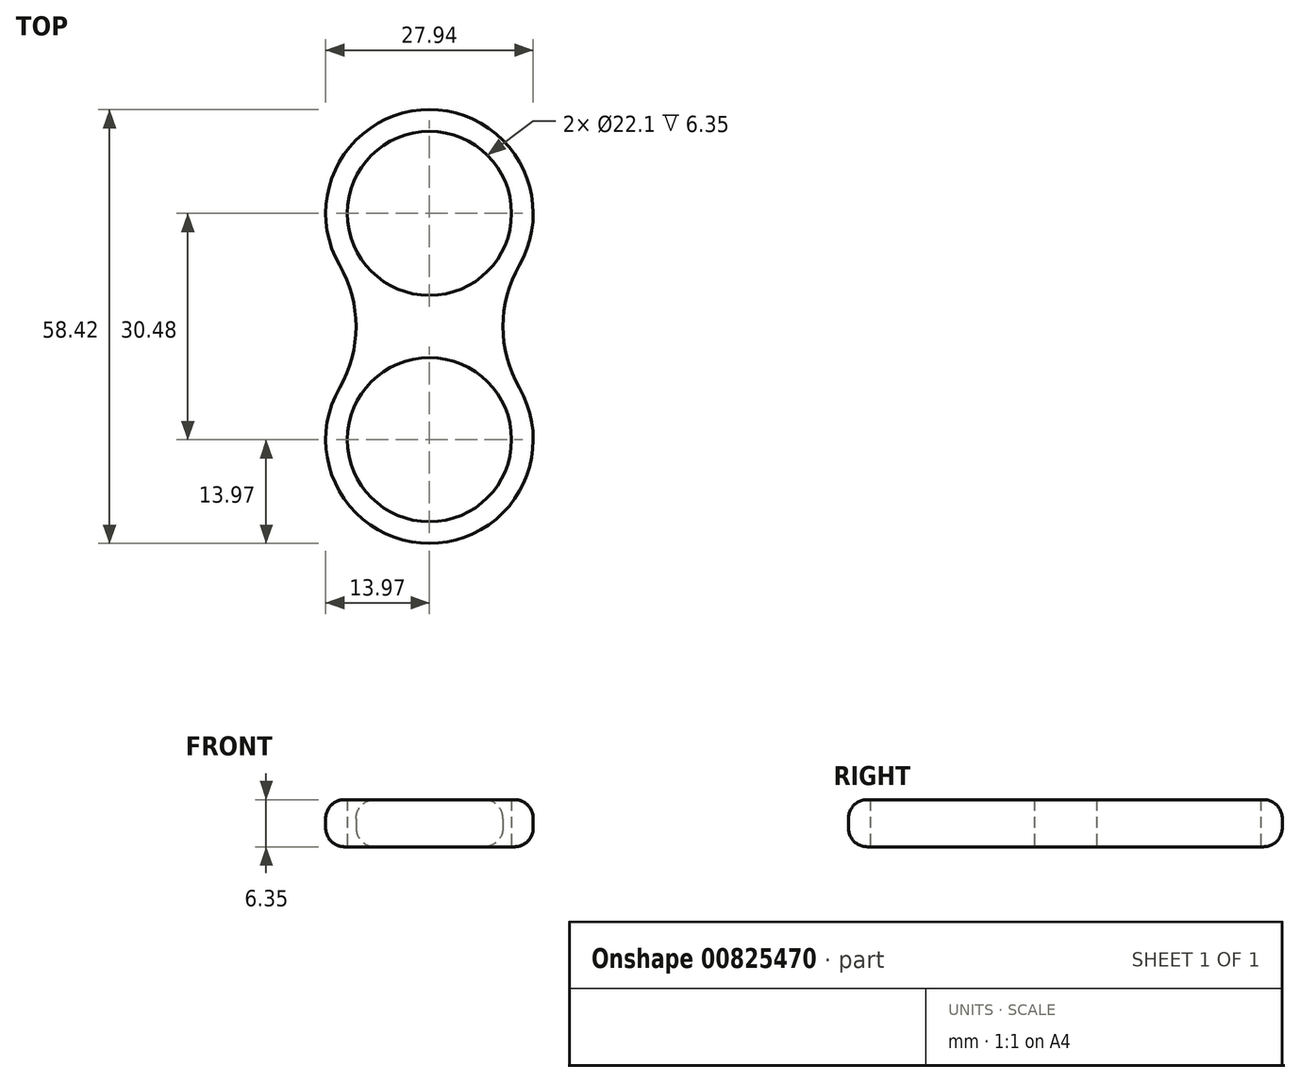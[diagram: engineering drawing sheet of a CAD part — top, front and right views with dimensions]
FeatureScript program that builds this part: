
annotation { "Feature Type Name" : "Feature", "Feature Type Description" : "" }
export const myFeature = defineFeature(function(context is Context, id is Id, definition is map)
    precondition{}
    {
        {
            var Q0;
            Q0=qCreatedBy(makeId("Top.planeOp"),FACE);
            var sketch = newSketch(context, id + "F0", { "sketchPlane" : qUnion([Q0])});
            skCircle(sketch, "E0", {"center": v(0, 0) * mm, "radius": 11.05 * mm});
            skArc(sketch, "E1", {"start": v(-12.1, 6.99) * mm, "mid": v(0, -13.97) * mm, "end": v(12.1, 6.99) * mm});
            skCircle(sketch, "E2", {"center": v(0, 30.48) * mm, "radius": 11.05 * mm});
            skArc(sketch, "E3", {"start": v(12.1, 23.5) * mm, "mid": v(0, 44.45) * mm, "end": v(-12.1, 23.5) * mm});
            skArc(sketch, "E4.trimOffspring", {"start": v(-12.1, 6.98) * mm, "mid": v(-9.89, 15.24) * mm, "end": v(-12.1, 23.5) * mm});
            skArc(sketch, "E5", {"start": v(12.1, 23.5) * mm, "mid": v(9.89, 15.24) * mm, "end": v(12.1, 6.99) * mm});
            skSolve(sketch);
        }
        {
            var Q0;
            Q0=makeQuery(id+"F0.imprint","IMPRINT",FACE,{"disambiguationData":[TD([[makeQuery(id+"F0.imprint","IMPRINT",EDGE,{"derivedFrom":sQuery(id+"F0.wireOp",EDGE,"E0")}),-1.0]])]});
            extrude(context, id + "F1", {"entities" : qUnion([Q0]), "depth" : 6.35 * mm, "offsetDistance" : 25.4 * mm});
        }
        {
            var Q0;
            Q0=makeQuery(id+"F1.opExtrude","CAP_EDGE",EDGE,{"disambiguationData":[OSD([sQuery(id+"F0.wireOp",EDGE,"E1")])],"isStart":false});
            fillet(context, id + "F2", {"entities" : qUnion([Q0]), "radius" : 2.54 * mm, "tangentPropagation" : true, "allowEdgeOverflow" : false});
        }
        {
            var Q0;
            Q0=makeQuery(id+"F1.opExtrude","CAP_EDGE",EDGE,{"disambiguationData":[OSD([sQuery(id+"F0.wireOp",EDGE,"E1")])],"isStart":true});
            fillet(context, id + "F3", {"entities" : qUnion([Q0]), "radius" : 2.54 * mm, "tangentPropagation" : true, "allowEdgeOverflow" : false});
        }
    });
